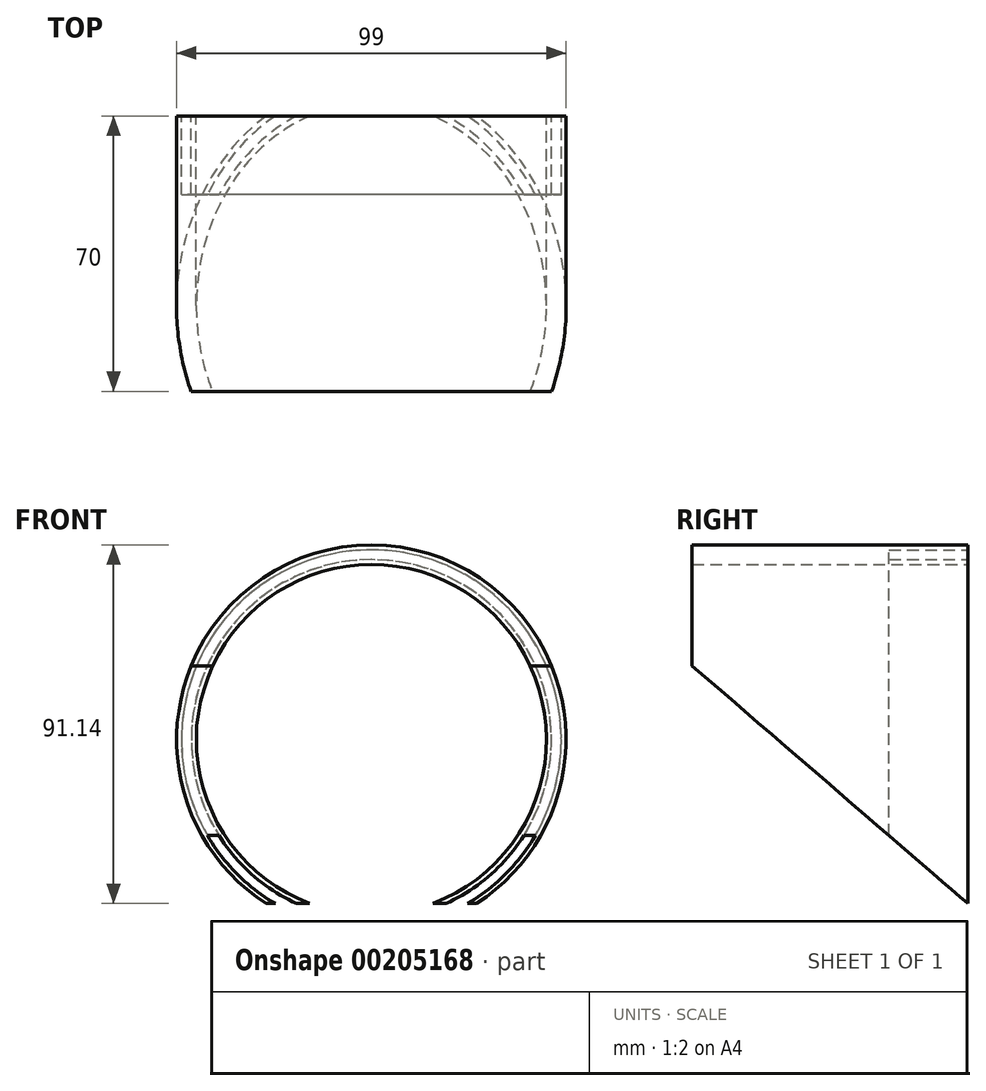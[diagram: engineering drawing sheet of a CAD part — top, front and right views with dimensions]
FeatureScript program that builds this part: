
annotation { "Feature Type Name" : "Feature", "Feature Type Description" : "" }
export const myFeature = defineFeature(function(context is Context, id is Id, definition is map)
    precondition{}
    {
        {
            var Q0;
            Q0=qCreatedBy(makeId("Front.planeOp"),FACE);
            var sketch = newSketch(context, id + "F0", { "sketchPlane" : qUnion([Q0])});
            skCircle(sketch, "E0", {"center": v(0, 0) * mm, "radius": 45.75 * mm});
            skCircle(sketch, "E1", {"center": v(0, 0) * mm, "radius": 48.25 * mm});
            skSolve(sketch);
        }
        {
            var Q0;
            Q0=qCreatedBy(makeId("Front.planeOp"),FACE);
            cPlane(context, id + "F1", {"entities" : qUnion([Q0]), "cplaneType" : CPlaneType.OFFSET, "offset" : 30 * mm, "width" : 150 * mm, "height" : 150 * mm});
        }
        {
            var Q0;
            Q0=qCreatedBy(id+"F1.planeOp",FACE);
            var sketch = newSketch(context, id + "F2", { "sketchPlane" : qUnion([Q0])});
            skCircle(sketch, "E2", {"center": v(0, 0) * mm, "radius": 44.5 * mm});
            skCircle(sketch, "E3", {"center": v(0, 0) * mm, "radius": 49.5 * mm});
            skSolve(sketch);
        }
        {
            var Q0;
            Q0 = qSketchRegion(id + "F2", true);
            extrude(context, id + "F3", {"entities" : qUnion([Q0]), "depth" : 70 * mm});
        }
        {
            var Q0;
            Q0 = qSketchRegion(id + "F0", true);
            extrude(context, id + "F4", {"entities" : qUnion([Q0]), "operationType" : NewBodyOperationType.REMOVE, "depth" : 50 * mm});
        }
        {
            var Q0;
            Q0=qCreatedBy(makeId("Right.planeOp"),FACE);
            var sketch = newSketch(context, id + "F5", { "sketchPlane" : qUnion([Q0])});
            skLineSegment(sketch, "E4", {"start": v(15.67, -81.06) * mm, "end": v(-147.62, 59.9) * mm});
            skLineSegment(sketch, "E5", {"start": v(-147.62, 59.9) * mm, "end": v(-147.62, -80.11) * mm});
            skLineSegment(sketch, "E6", {"start": v(-147.62, -80.11) * mm, "end": v(15.67, -81.06) * mm});
            skSolve(sketch);
        }
        {
            var Q0;
            Q0 = qSketchRegion(id + "F5", true);
            extrude(context, id + "F6", {"entities" : qUnion([Q0]), "operationType" : NewBodyOperationType.REMOVE, "endBound" : BoundingType.SYMMETRIC, "oppositeDirection" : true, "depth" : 120 * mm});
        }
    });
